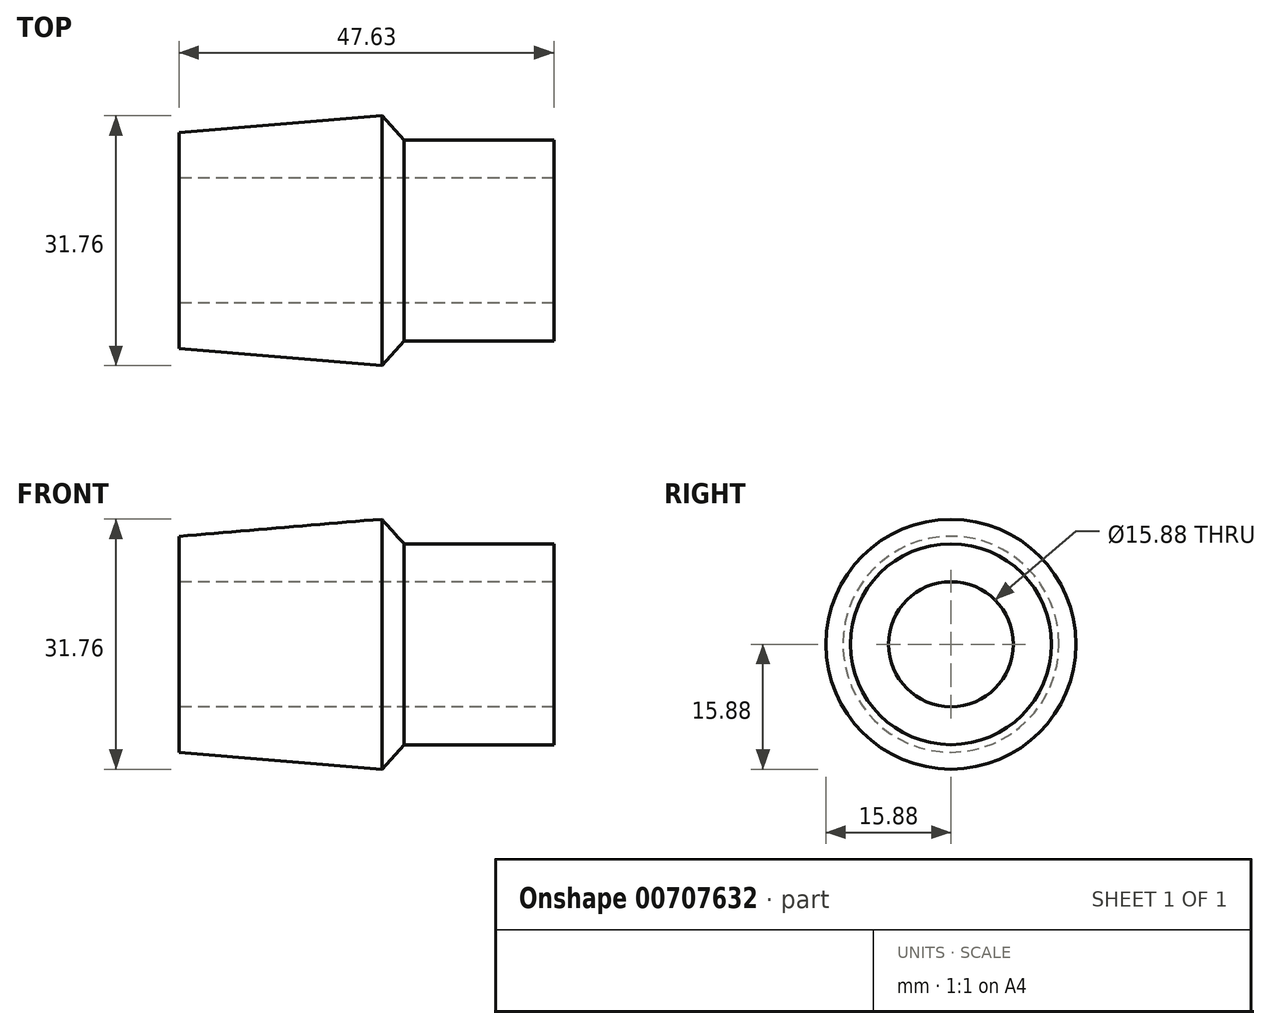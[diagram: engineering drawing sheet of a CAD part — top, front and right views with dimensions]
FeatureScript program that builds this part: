
annotation { "Feature Type Name" : "Feature", "Feature Type Description" : "" }
export const myFeature = defineFeature(function(context is Context, id is Id, definition is map)
    precondition{}
    {
        {
            var Q0;
            Q0=qCreatedBy(makeId("Front.planeOp"),FACE);
            var sketch = newSketch(context, id + "F0", { "sketchPlane" : qUnion([Q0])});
            skLineSegment(sketch, "E0", {"start": v(-31.88, 0) * mm, "end": v(26.1, 0) * mm, "construction": true});
            skLineSegment(sketch, "E1", {"start": v(0, 13.72) * mm, "end": v(25.78, 15.88) * mm});
            skLineSegment(sketch, "E2", {"start": v(25.78, 15.88) * mm, "end": v(28.58, 12.76) * mm});
            skLineSegment(sketch, "E3", {"start": v(28.58, 12.76) * mm, "end": v(47.63, 12.76) * mm});
            skLineSegment(sketch, "E4", {"start": v(47.63, 12.76) * mm, "end": v(47.63, 7.94) * mm});
            skLineSegment(sketch, "E5", {"start": v(47.63, 7.94) * mm, "end": v(0, 7.94) * mm});
            skLineSegment(sketch, "E6", {"start": v(0, 7.94) * mm, "end": v(0, 13.72) * mm});
            skSolve(sketch);
        }
        {
            var Q0;
            Q0=makeQuery(id+"F0.imprint","IMPRINT",FACE,{"disambiguationData":[TD([[makeQuery(id+"F0.imprint","IMPRINT",EDGE,{"derivedFrom":sQuery(id+"F0.wireOp",EDGE,"E1")}),-1.0]])]});
            var Q1;
            Q1=sQuery(id+"F0.wireOp",EDGE,"E0");
            revolve(context, id + "F1", {"entities" : qUnion([Q0]), "axis" : qUnion([Q1]), "revolveType" : RevolveType.FULL});
        }
    });
